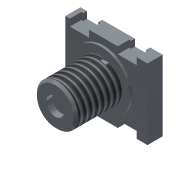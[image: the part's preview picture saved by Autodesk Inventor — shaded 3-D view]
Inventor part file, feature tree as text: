
AUTODESK INVENTOR PART (.ipt)
format: ipt  version: 2014 (Build 180170000, 170)  size: 224,256 bytes
history: native  units: in
note: dims shown in document units (in); Inventor stores cm internally (conversion verified against a paired STEP export)
features: sketch x9, extrude x8, reference x2, thread x1, chamfer x1, plane x1, revolve x1
ambient origin geometry x8: Origin, YZ Plane, XZ Plane, XY Plane, X Axis, Y Axis, Z Axis, Center Point
bodies: Solid1 (feature_tree)
feature tree (23):
  extrude  "Extrusion1"  Depth=0.464in
  extrude  "Extrusion2"  Depth=0.1in
  thread  "Thread1"  [1 undecoded]
  extrude  "Extrusion3"  Depth=0.315in
  chamfer  "Chamfer1"  Distance=0.315in
  plane  "Work Plane1"
  revolve  "Revolution1"  [1 undecoded]
  extrude  "Extrusion4"  Depth=0.015in TaperAngle=45.0deg
  extrude  "Extrusion5"  Depth=0.01in
  extrude  "Extrusion6"  TaperAngle=90.0deg  [1 undecoded]
  extrude  "Extrusion7"  Depth=0.04in TaperAngle=0.0deg
  extrude  "Extrusion8"  Depth=0.125in
  sketch  "Sketch1"  dims[d0=0.54in d1=0.464in]
  sketch  "Sketch2"  dims[d2=0.1in d3=0.0in d4=0.272in d5=0.29in]
  sketch  "Sketch3"  dims[d6=0.464in d7=0.232in d8=0.315in d9=0.0in]
  sketch  "Sketch4"  dims[d10=1.0in d11=0.0in d12=0.38in]
  sketch  "Sketch5"  dims[d13=0.015in d14=0.0in d15=0.015in d16=0.125in d17=45.0deg]
  sketch  "Sketch6"  dims[d18=0.29in d19=0.01in]
  reference  "Reference1"
  reference  "Reference2"
  sketch  "Sketch7"  dims[d20=0.025in d21=90.0deg]
  sketch  "Sketch8"  dims[d22=0.118in d23=0.04in d24=0.0in]
  sketch  "Sketch9"  dims[d25=0.125in d26=0.125in d27=0.125in d28=0.125in d29=0.54in d30=0.44in d32=0.045in d33=0.045in d34=0.19in d35=0.03in d36=0.075in d37=0.0in d38=0.125in d39=0.1in d40=0.0125in d41=0.075in d42=0.0in d43=0.1in d44=0.125in d45=0.0125in d46=0.075in d47=0.0in d48=0.1in d49=0.125in d50=0.0125in d51=0.0125in d52=0.075in d53=0.0in]
note: 3 required parameter values undecoded (feature->parameter linkage not recoverable at this tier; creation-order binding heuristic only, values carry confidence <= 0.55)